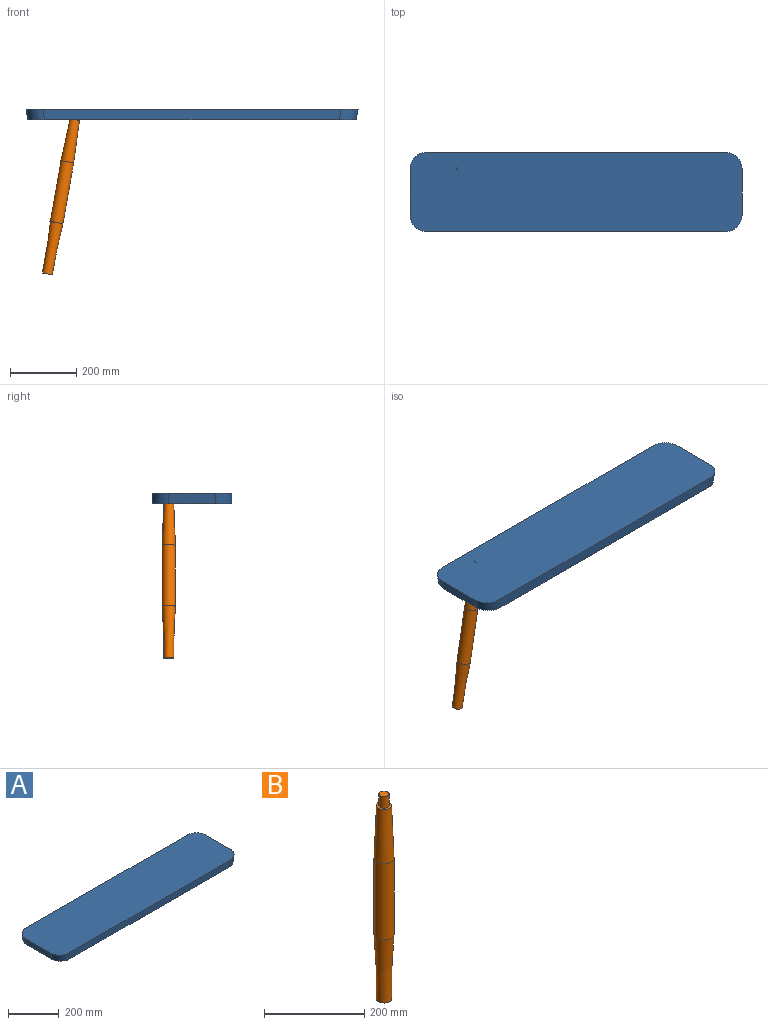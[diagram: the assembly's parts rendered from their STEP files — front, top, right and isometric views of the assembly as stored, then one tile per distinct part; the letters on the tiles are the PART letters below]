
ASSEMBLY  parts=2 mates=1
PART A: 12 faces, bbox 1000x240x48.4 mm
  f0: plane 1000x240mm, normal (0,0,1), area 237820.9mm2, adj f1,f3,f4,f5,f6,f7,f8,f9
  f1: plane 140x31mm, normal (-0.98,0,-0.17), area 4407mm2, adj f0,f2,f8,f9
  f2: plane 989.07x240mm, normal (0,0,-1), area 234878.1mm2, adj f1,f3,f4,f5,f6,f7,f8,f9
  f3: plane 140x31mm, normal (0.98,0,-0.17), area 4407mm2, adj f0,f2,f6,f7
  f4: plane 898.46x31mm, normal (0,-1,0), area 27682.7mm2, adj f0,f2,f6,f8
  f5: plane 898.46x31mm, normal (0,1,0), area 27682.7mm2, adj f0,f2,f7,f9
  f6: cylinder r=50mm len=56.24mm, axis (-0.17,0,-0.98), area 2472.3mm2, adj f0,f2,f3,f4
  f7: cylinder r=50mm len=56.24mm, axis (-0.17,0,-0.98), area 2472.3mm2, adj f0,f2,f3,f5
  f8: cylinder r=50mm len=56.24mm, axis (-0.17,0,0.98), area 2472.3mm2, adj f0,f1,f2,f4
  f9: cylinder r=50mm len=56.24mm, axis (-0.17,0,0.98), area 2472.3mm2, adj f0,f1,f2,f5
  f10: cylinder r=10mm len=26.23mm, axis (0.17,0,0.98), area 1339.8mm2, adj f2,f11
  f11: plane 20x19.7mm, normal (-0.17,0,-0.98), area 314.2mm2, adj f10
PART B: 7 faces, bbox 40x40x500 mm
  f0: revolved ~129.05x40mm, area 14200.9mm2, adj f1,f6
  f1: plane 30x30mm, normal (0,0,1), area 392.7mm2, adj f0,f2
  f2: cylinder r=10mm len=28mm, axis (0,0,1), area 1759.3mm2, adj f1,f3
  f3: plane 20x20mm, normal (0,0,1), area 314.2mm2, adj f2
  f4: plane 30x30mm, normal (0,0,-1), area 706.9mm2, adj f5
  f5: revolved ~157.05x40mm, area 16236.6mm2, adj f4,f6
  f6: cylinder r=20mm len=185.89mm, axis (0,0,1), area 23359.9mm2, adj f0,f5
PLACE A at identity fixed
PLACE B rot(axis=(0,1,0),10deg) t=(-392.25,70,-175.05)mm
MATE ball A.f2 <-> B.f2  axis (0,0,-1) through (-353.7,70,43.58)mm
